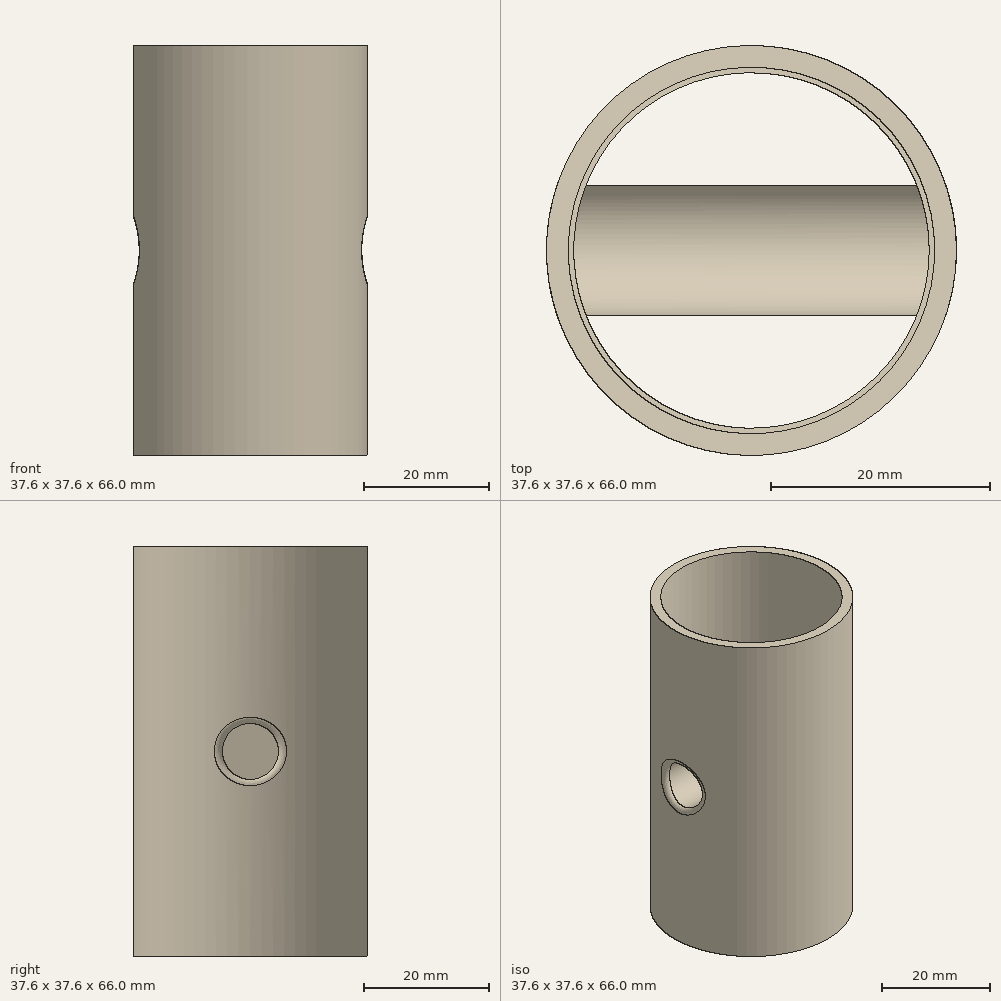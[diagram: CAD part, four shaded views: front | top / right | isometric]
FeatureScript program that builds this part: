
annotation { "Feature Type Name" : "Feature", "Feature Type Description" : "" }
export const myFeature = defineFeature(function(context is Context, id is Id, definition is map)
    precondition{}
    {
        {
            var Q0;
            Q0=qCreatedBy(makeId("Top.planeOp"),FACE);
            var sketch = newSketch(context, id + "F0", { "sketchPlane" : qUnion([Q0])});
            skCircle(sketch, "E0", {"center": v(0, 0) * mm, "radius": 16.8 * mm});
            skCircle(sketch, "E1", {"center": v(0, 0) * mm, "radius": 18.8 * mm});
            skCircle(sketch, "E2", {"center": v(0, 0) * mm, "radius": 16.3 * mm});
            skSolve(sketch);
        }
        {
            var Q0;
            Q0=makeQuery(id+"F0.imprint","IMPRINT",FACE,{"disambiguationData":[TD([[makeQuery(id+"F0.imprint","IMPRINT",EDGE,{"derivedFrom":sQuery(id+"F0.wireOp",EDGE,"E0")}),-1.0]])]});
            extrude(context, id + "F1", {"entities" : qUnion([Q0]), "depth" : 66 * mm, "offsetDistance" : 25 * mm});
        }
        {
            var Q0;
            Q0=qCreatedBy(makeId("Right.planeOp"),FACE);
            var sketch = newSketch(context, id + "F2", { "sketchPlane" : qUnion([Q0])});
            skLineSegment(sketch, "E3", {"start": v(0, 0) * mm, "end": v(0, 33) * mm, "construction": true});
            skCircle(sketch, "E4", {"center": v(0, 33) * mm, "radius": 4.5 * mm});
            skCircle(sketch, "E5", {"center": v(0, 33) * mm, "radius": 6 * mm});
            skSolve(sketch);
        }
        {
            var Q0;
            Q0=makeQuery(id+"F2.imprint","IMPRINT",FACE,{"disambiguationData":[TD([[makeQuery(id+"F2.imprint","IMPRINT",EDGE,{"derivedFrom":sQuery(id+"F2.wireOp",EDGE,"E4")}),1.0]])]});
            extrude(context, id + "F3", {"entities" : qUnion([Q0]), "operationType" : NewBodyOperationType.REMOVE, "endBound" : BoundingType.SYMMETRIC, "oppositeDirection" : true, "depth" : 40 * mm, "offsetDistance" : 25 * mm});
        }
        {
            var Q0;
            Q0=makeQuery(id+"F2.imprint","IMPRINT",FACE,{"disambiguationData":[TD([[makeQuery(id+"F2.imprint","IMPRINT",EDGE,{"derivedFrom":sQuery(id+"F2.wireOp",EDGE,"E4")}),-1.0]])]});
            extrude(context, id + "F4", {"entities" : qUnion([Q0]), "operationType" : NewBodyOperationType.ADD, "endBound" : BoundingType.SYMMETRIC, "depth" : 35.5 * mm, "offsetDistance" : 25 * mm});
        }
        {
            var Q0;
            Q0=makeQuery(id+"F2.imprint","IMPRINT",FACE,{"disambiguationData":[TD([[makeQuery(id+"F2.imprint","IMPRINT",EDGE,{"derivedFrom":sQuery(id+"F2.wireOp",EDGE,"E4")}),1.0]])]});
            extrude(context, id + "F5", {"entities" : qUnion([Q0]), "operationType" : NewBodyOperationType.ADD, "depth" : 2 * mm, "offsetDistance" : 25 * mm});
        }
        {
            var Q0;
            Q0=makeQuery(id+"F3.boolean.opBoolean","INTERSECT",EDGE,{"disambiguationData":[OD(0.0)],"derivedFrom":[makeQuery(id+"F1.opExtrude","SWEPT_FACE",FACE,{"disambiguationData":[OSD([sQuery(id+"F0.wireOp",EDGE,"E1")])]}),makeQuery(id+"F3.opExtrude","SWEPT_FACE",FACE,{"disambiguationData":[OSD([sQuery(id+"F2.wireOp",EDGE,"E4")])]})]});
            var Q1;
            Q1=makeQuery(id+"F3.boolean.opBoolean","INTERSECT",EDGE,{"disambiguationData":[OD(1.0)],"derivedFrom":[makeQuery(id+"F1.opExtrude","SWEPT_FACE",FACE,{"disambiguationData":[OSD([sQuery(id+"F0.wireOp",EDGE,"E1")])]}),makeQuery(id+"F3.opExtrude","SWEPT_FACE",FACE,{"disambiguationData":[OSD([sQuery(id+"F2.wireOp",EDGE,"E4")])]})]});
            fillet(context, id + "F6", {"entities" : qUnion([Q0, Q1]), "radius" : 1 * mm, "tangentPropagation" : true, "allowEdgeOverflow" : false});
        }
        {
            var Q0;
            Q0=makeQuery(id+"F0.imprint","IMPRINT",FACE,{"disambiguationData":[TD([[makeQuery(id+"F0.imprint","IMPRINT",EDGE,{"derivedFrom":sQuery(id+"F0.wireOp",EDGE,"E0")}),1.0]])]});
            extrude(context, id + "F7", {"entities" : qUnion([Q0]), "operationType" : NewBodyOperationType.ADD, "depth" : 23 * mm, "offsetDistance" : 25 * mm});
        }
        {
            var Q0;
            Q0=makeQuery(id+"F0.imprint","IMPRINT",FACE,{"disambiguationData":[TD([[makeQuery(id+"F0.imprint","IMPRINT",EDGE,{"derivedFrom":sQuery(id+"F0.wireOp",EDGE,"E0")}),1.0]])]});
            extrude(context, id + "F8", {"entities" : qUnion([Q0]), "operationType" : NewBodyOperationType.REMOVE, "depth" : 22 * mm, "offsetDistance" : 25 * mm});
        }
        {
            var Q0;
            Q0=makeQuery(id+"F1.opExtrude","CAP_FACE",FACE,{"disambiguationData":[OSD([sQuery(id+"F0.wireOp",EDGE,"E0"),sQuery(id+"F0.wireOp",EDGE,"E1")])],"isStart":false});
            var sketch = newSketch(context, id + "F9", { "sketchPlane" : qUnion([Q0])});
            skCircle(sketch, "E6", {"center": v(0, 0) * mm, "radius": 16.3 * mm});
            skCircle(sketch, "E7", {"center": v(0, 0) * mm, "radius": 16.8 * mm});
            skSolve(sketch);
        }
        {
            var Q0;
            Q0=makeQuery(id+"F9.imprint","IMPRINT",FACE,{"disambiguationData":[TD([[makeQuery(id+"F9.imprint","IMPRINT",EDGE,{"derivedFrom":sQuery(id+"F9.wireOp",EDGE,"E6")}),-1.0]])]});
            extrude(context, id + "F10", {"entities" : qUnion([Q0]), "operationType" : NewBodyOperationType.ADD, "oppositeDirection" : true, "depth" : 23 * mm, "offsetDistance" : 25 * mm});
        }
        {
            var Q0;
            Q0=makeQuery(id+"F9.imprint","IMPRINT",FACE,{"disambiguationData":[TD([[makeQuery(id+"F9.imprint","IMPRINT",EDGE,{"derivedFrom":sQuery(id+"F9.wireOp",EDGE,"E6")}),-1.0]])]});
            extrude(context, id + "F11", {"entities" : qUnion([Q0]), "operationType" : NewBodyOperationType.REMOVE, "oppositeDirection" : true, "depth" : 22 * mm, "offsetDistance" : 25 * mm});
        }
    });
